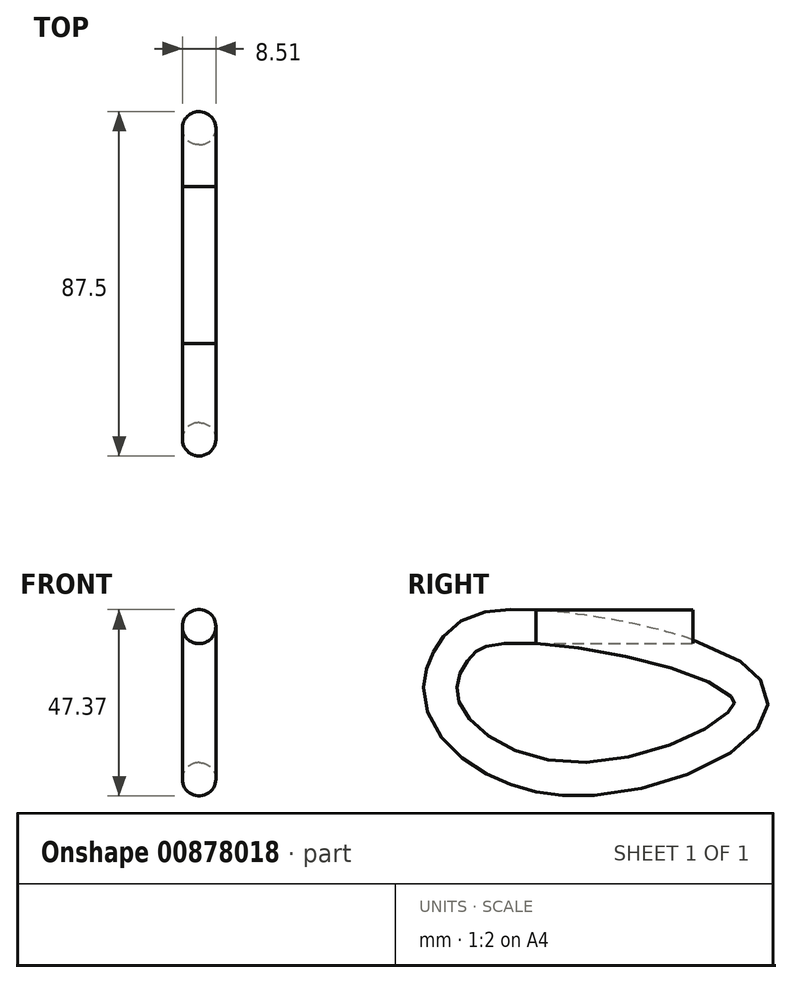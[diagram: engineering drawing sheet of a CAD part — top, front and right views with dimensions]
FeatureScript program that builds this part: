
annotation { "Feature Type Name" : "Feature", "Feature Type Description" : "" }
export const myFeature = defineFeature(function(context is Context, id is Id, definition is map)
    precondition{}
    {
        {
            var Q0;
            Q0=qCreatedBy(makeId("Front.planeOp"),FACE);
            var sketch = newSketch(context, id + "F0", { "sketchPlane" : qUnion([Q0])});
            skCircle(sketch, "E0", {"center": v(-24.33, 35.05) * mm, "radius": 4.25 * mm});
            skSolve(sketch);
        }
        {
            var Q0;
            Q0=makeQuery(id+"F0.imprint","IMPRINT",FACE,{"disambiguationData":[TD([[makeQuery(id+"F0.imprint","IMPRINT",EDGE,{"derivedFrom":sQuery(id+"F0.wireOp",EDGE,"E0")}),1.0]])]});
            extrude(context, id + "F1", {"entities" : qUnion([Q0]), "depth" : 39.88 * mm, "offsetDistance" : 25.4 * mm});
        }
        {
            var Q0;
            Q0=qCreatedBy(makeId("Right.planeOp"),FACE);
            var sketch = newSketch(context, id + "F2", { "sketchPlane" : qUnion([Q0])});
            skPoint(sketch, "E1.first.point", {"position": v(55.89, 33.07) * mm});
            skPoint(sketch, "E1.second.point", {"position": v(14.84, 17.27) * mm});
            skPoint(sketch, "E1.third.point", {"position": v(31.42, 36) * mm});
            skFitSpline(sketch, "E2", {"points": [v(-44.72, 35.42) * mm, v(-60.47, 29.68) * mm, v(-63.83, 15.2) * mm, v(-29.48, -3.87) * mm, v(14.84, 17.27) * mm, v(-44.72, 35.42) * mm]});
            skSolve(sketch);
        }
        {
            var Q0;
            Q0=makeQuery(id+"F1.opExtrude","CAP_FACE",FACE,{"disambiguationData":[OSD([sQuery(id+"F0.wireOp",EDGE,"E0")])],"isStart":false});
            var Q1;
            Q1=sQuery(id+"F2.wireOp",EDGE,"E2");
            sweep(context, id + "F3", {"profiles" : qUnion([Q0]), "path" : qUnion([Q1])});
        }
    });
